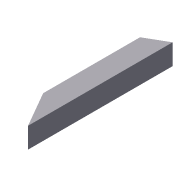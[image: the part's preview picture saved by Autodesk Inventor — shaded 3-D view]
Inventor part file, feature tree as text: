
AUTODESK INVENTOR PART (.ipt)
format: ipt  version: 2012 (Build 160160000, 160)  size: 84,480 bytes
history: native  units: in
note: dims shown in document units (in); Inventor stores cm internally (conversion verified against a paired STEP export)
features: extrude x2, sketch x2, shell x1
ambient origin geometry x8: Origin, YZ Plane, XZ Plane, XY Plane, X Axis, Y Axis, Z Axis, Center Point
bodies: Solid1 (feature_tree)
feature tree (5):
  extrude  "Extrusion1"  Depth=1.0in
  shell  "Shell1"  Thickness=7.0in
  extrude  "Extrusion2"  TaperAngle=60.0deg  [1 undecoded]
  sketch  "Sketch1"  dims[d0=1.0in d1=1.0in d2=7.0in d3=0.0in]
  sketch  "Sketch2"  dims[d4=0.0625in d5=60.0deg d6=30.0deg d7=11.0in d8=0.0in]
note: 1 required parameter value undecoded (feature->parameter linkage not recoverable at this tier; creation-order binding heuristic only, values carry confidence <= 0.55)
